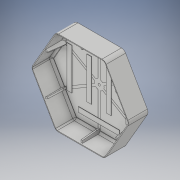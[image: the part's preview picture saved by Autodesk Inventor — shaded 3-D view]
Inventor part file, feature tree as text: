
AUTODESK INVENTOR PART (.ipt)
format: ipt  version: 2019 (Build 230136000, 136)  size: 369,152 bytes
history: native  units: mm
features: sketch x8, extrude x5, plane x3, fillet x3, other x3, projected_geometry x3, shell x1, pattern_circular x1
ambient origin geometry x8: Origin, YZ Plane, XZ Plane, XY Plane, X Axis, Y Axis, Z Axis, Center Point
bodies: Solid1 (feature_tree)
feature tree (27):
  extrude  "Extrusion1"  Depth=40.0mm TaperAngle=0.0deg
  shell  "Shell1"  Thickness=1.5mm
  extrude  "Extrusion9"  Depth=10.0mm
  plane  "Work Plane1"
  plane  "Work Plane2"
  plane  "Work Plane3"
  extrude  "Extrusion5"  Depth=5.0mm
  extrude  "Extrusion6"  TaperAngle=60.0deg  [1 undecoded]
  extrude  "Extrusion8"  TaperAngle=90.0deg  [1 undecoded]
  pattern_circular  "Circular Pattern1"  [2 undecoded]
  fillet  "Fillet1"  Radius=3.0mm
  fillet  "Fillet2"  Radius=8.0mm
  fillet  "Fillet4"  Radius=36.0mm
  sketch  "Sketch5"  dims[d12=1.0mm d37=5.0mm]
  sketch  "Sketch6"  dims[d44=10.0mm d45=60.0deg]
  sketch  "Sketch7"  dims[d46=90.0deg d47=90.0deg]
  other  "Work Axis4"
  other  "Work Axis5"
  other  "Work Axis6"
  sketch  "Sketch1"  dims[d0=175.0mm d2=40.0mm d3=0.0mm d4=1.5mm]
  sketch  "Sketch4"  dims[d10=4.0mm d11=10.0mm]
  projected_geometry  "Projected Loop3"
  sketch  "Sketch8"  dims[d52=5.5mm]
  projected_geometry  "Projected Loop4"
  sketch  "Sketch9"  dims[d53=0.01mm d54=0.0mm]
  projected_geometry  "Projected Loop5"
  sketch  "Sketch11"  dims[d55=5.0mm d56=2.0mm d57=3.0mm d58=8.0mm d59=36.0mm d60=0.0mm d70=60.0mm d72=360.0deg d74=60.0mm d75=360.0deg d77=3.0mm d78=30.0mm d79=20.0mm d80=0.0mm d138=10.0mm d139=85.0mm d140=40.0mm d142=40.5mm d143=10.0mm d145=10.0mm d147=130.0mm d149=0.75mm d150=0.0mm]
note: 4 required parameter values undecoded (feature->parameter linkage not recoverable at this tier; creation-order binding heuristic only, values carry confidence <= 0.55)
